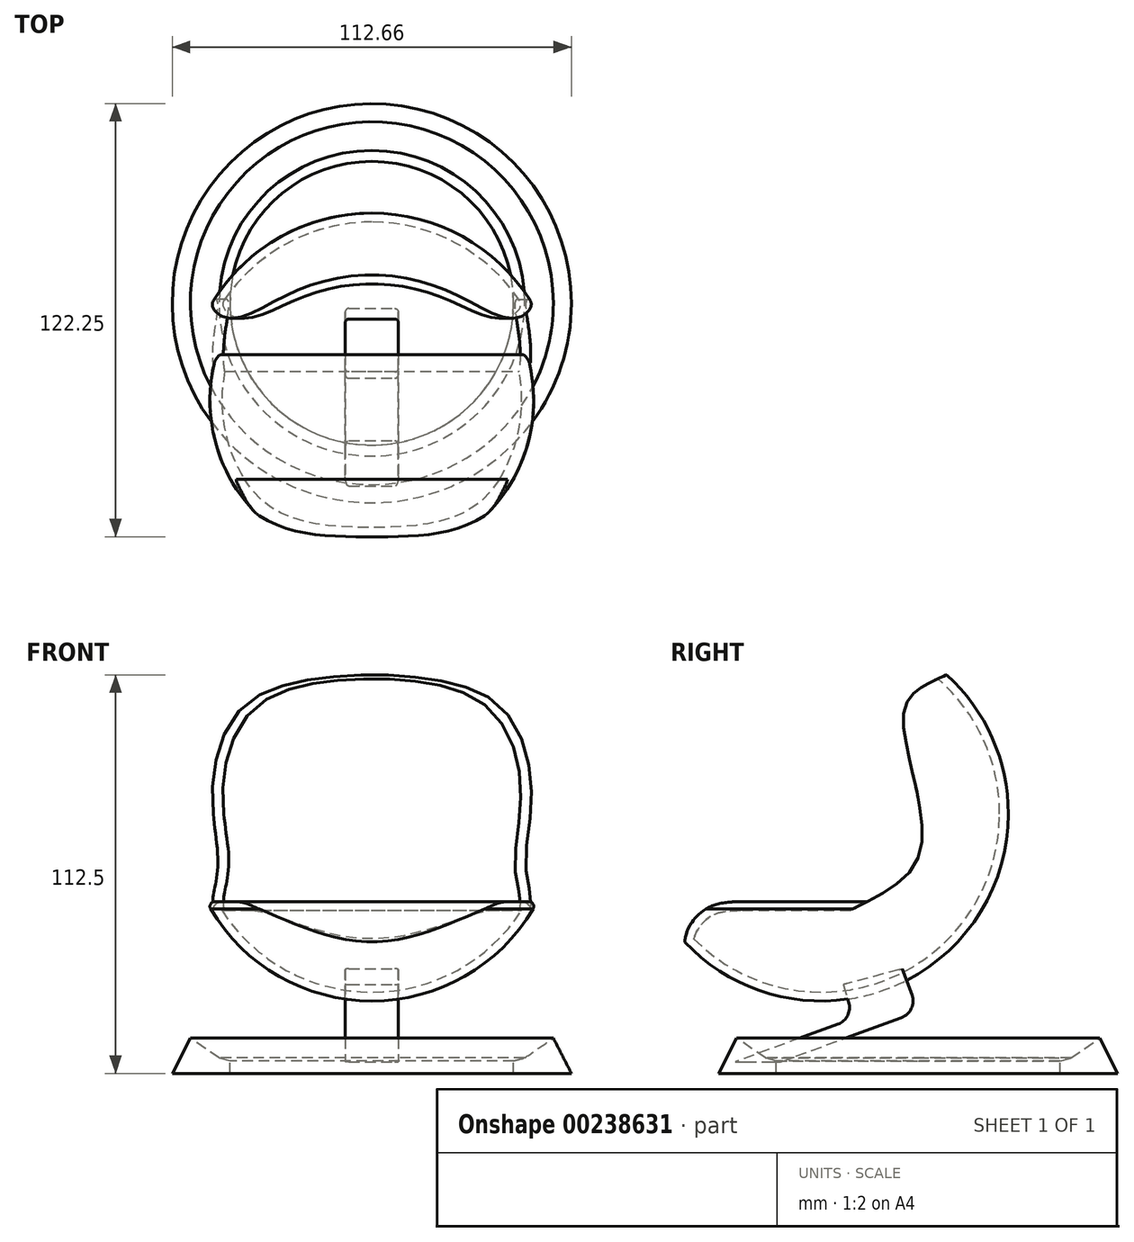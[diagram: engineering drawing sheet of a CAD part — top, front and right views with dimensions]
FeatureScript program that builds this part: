
annotation { "Feature Type Name" : "Feature", "Feature Type Description" : "" }
export const myFeature = defineFeature(function(context is Context, id is Id, definition is map)
    precondition{}
    {
        {
            var Q0;
            Q0=qCreatedBy(makeId("Top.planeOp"),FACE);
            var sketch = newSketch(context, id + "F0", { "sketchPlane" : qUnion([Q0])});
            skArc(sketch, "E0", {"start": v(0, 52.85) * mm, "mid": v(-52.85, 0) * mm, "end": v(0, -52.85) * mm});
            skLineSegment(sketch, "E1", {"start": v(0, -52.85) * mm, "end": v(0, 52.85) * mm});
            skSolve(sketch);
        }
        {
            var Q0;
            Q0=makeQuery(id+"F0.imprint","IMPRINT",FACE,{"disambiguationData":[TD([[makeQuery(id+"F0.imprint","IMPRINT",EDGE,{"derivedFrom":sQuery(id+"F0.wireOp",EDGE,"E0")}),1.0]])]});
            var Q1;
            Q1=sQuery(id+"F0.wireOp",EDGE,"E1");
            revolve(context, id + "F1", {"entities" : qUnion([Q0]), "axis" : qUnion([Q1]), "revolveType" : RevolveType.FULL});
        }
        {
            var Q0;
            Q0=qCreatedBy(makeId("Right.planeOp"),FACE);
            var sketch = newSketch(context, id + "F2", { "sketchPlane" : qUnion([Q0])});
            skFitSpline(sketch, "E2", {"points": [v(-34.6, -49.13) * mm, v(-38.42, -35.34) * mm, v(-31.97, -26.54) * mm, v(-22.3, -24.78) * mm], "startDerivative": vector(-18.06, 38.54) * mm, "endDerivative": vector(32.71, 0.77) * mm});
            skLineSegment(sketch, "E3", {"start": v(-22.3, -24.78) * mm, "end": v(12.9, -24.78) * mm});
            skFitSpline(sketch, "E4", {"points": [v(12.9, -24.78) * mm, v(28.16, -9.83) * mm, v(23.17, 26.54) * mm, v(28.74, 35.93) * mm, v(50.15, 44.43) * mm], "startDerivative": vector(83.43, 43.93) * mm, "endDerivative": vector(95.72, 31.54) * mm});
            skLineSegment(sketch, "E5", {"start": v(50.15, 44.43) * mm, "end": v(14.37, 64.97) * mm});
            skLineSegment(sketch, "E6", {"start": v(14.37, 64.97) * mm, "end": v(-80.66, 51.77) * mm});
            skLineSegment(sketch, "E7", {"start": v(-80.66, 51.77) * mm, "end": v(-54.55, -56.17) * mm});
            skLineSegment(sketch, "E8", {"start": v(-54.55, -56.17) * mm, "end": v(-34.6, -49.13) * mm});
            skSolve(sketch);
        }
        {
            var Q0;
            Q0=makeQuery(id+"F2.imprint","IMPRINT",FACE,{"disambiguationData":[TD([[makeQuery(id+"F2.imprint","IMPRINT",EDGE,{"derivedFrom":sQuery(id+"F2.wireOp",EDGE,"E2")}),1.0]])]});
            extrude(context, id + "F3", {"entities" : qUnion([Q0]), "operationType" : NewBodyOperationType.REMOVE, "oppositeDirection" : true, "depth" : 114 * mm, "symmetric" : true});
        }
        {
            var Q0;
            Q0=makeQuery(id+"F3.boolean.opBoolean","COPY",FACE,{"derivedFrom":makeQuery(id+"F3.opExtrude","SWEPT_FACE",FACE,{"disambiguationData":[OSD([sQuery(id+"F2.wireOp",EDGE,"E4")])]})});
            shell(context, id + "F4", {"entities" : qUnion([Q0]), "thickness" : 2.5 * mm});
        }
        {
            var Q0;
            Q0=qCreatedBy(makeId("Right.planeOp"),FACE);
            var sketch = newSketch(context, id + "F5", { "sketchPlane" : qUnion([Q0])});
            skLineSegment(sketch, "E9", {"start": v(6.26, -48.22) * mm, "end": v(9.16, -57.76) * mm});
            skLineSegment(sketch, "E10", {"start": v(9.16, -57.76) * mm, "end": v(-24.23, -70) * mm});
            skLineSegment(sketch, "E11", {"start": v(-24.23, -70) * mm, "end": v(-11.37, -70) * mm});
            skLineSegment(sketch, "E12", {"start": v(-11.37, -70) * mm, "end": v(27.35, -55.8) * mm});
            skLineSegment(sketch, "E13", {"start": v(27.35, -55.8) * mm, "end": v(22.92, -43.74) * mm});
            skLineSegment(sketch, "E14", {"start": v(22.92, -43.74) * mm, "end": v(6.26, -48.22) * mm});
            skSolve(sketch);
        }
        {
            var Q0;
            Q0=makeQuery(id+"F5.imprint","IMPRINT",FACE,{"disambiguationData":[TD([[makeQuery(id+"F5.imprint","IMPRINT",EDGE,{"derivedFrom":sQuery(id+"F5.wireOp",EDGE,"E9")}),1.0]])]});
            extrude(context, id + "F6", {"entities" : qUnion([Q0]), "oppositeDirection" : true, "depth" : 15 * mm, "offsetDistance" : 25 * mm, "symmetric" : true});
        }
        {
            var Q0;
            Q0=qCreatedBy(makeId("Right.planeOp"),FACE);
            var sketch = newSketch(context, id + "F7", { "sketchPlane" : qUnion([Q0])});
            skLineSegment(sketch, "E15", {"start": v(-15.73, -68.93) * mm, "end": v(-23.82, -63.33) * mm});
            skLineSegment(sketch, "E16", {"start": v(27.4, -61.47) * mm, "end": v(27.4, -83.03) * mm, "construction": true});
            skLineSegment(sketch, "E17", {"start": v(-12.64, -73.29) * mm, "end": v(-28.93, -73.29) * mm});
            skLineSegment(sketch, "E18", {"start": v(-28.93, -73.29) * mm, "end": v(-23.82, -63.33) * mm});
            skPoint(sketch, "E19.start.orphan", {"position": v(-23.82, -83.03) * mm});
            skLineSegment(sketch, "E20", {"start": v(-12.64, -73.29) * mm, "end": v(-12.64, -69.73) * mm});
            skLineSegment(sketch, "E21", {"start": v(-12.64, -69.73) * mm, "end": v(-15.73, -68.93) * mm});
            skSolve(sketch);
        }
        {
            var Q0;
            Q0=makeQuery(id+"F7.imprint","IMPRINT",FACE,{"disambiguationData":[TD([[makeQuery(id+"F7.imprint","IMPRINT",EDGE,{"derivedFrom":sQuery(id+"F7.wireOp",EDGE,"E15")}),1.0]])]});
            var Q1;
            Q1=sQuery(id+"F7.wireOp",EDGE,"E16");
            revolve(context, id + "F8", {"entities" : qUnion([Q0]), "axis" : qUnion([Q1]), "revolveType" : RevolveType.FULL});
        }
        {
            var Q0;
            Q0=makeQuery(id+"F6.opExtrude","SWEPT_EDGE",EDGE,{"disambiguationData":[OSD([sQuery(id+"F5.wireOp",EDGE,"E9"),sQuery(id+"F5.wireOp",EDGE,"E10")])]});
            var Q1;
            Q1=makeQuery(id+"F6.opExtrude","SWEPT_EDGE",EDGE,{"disambiguationData":[OSD([sQuery(id+"F5.wireOp",EDGE,"E12"),sQuery(id+"F5.wireOp",EDGE,"E13")])]});
            fillet(context, id + "F9", {"entities" : qUnion([Q0, Q1]), "radius" : 5 * mm, "tangentPropagation" : true, "allowEdgeOverflow" : false});
        }
        {
            var Q0;
            Q0=makeQuery(id+"F6.opExtrude","CAP_EDGE",EDGE,{"disambiguationData":[OSD([sQuery(id+"F5.wireOp",EDGE,"E13")])],"isStart":true});
            var Q1;
            {var subQ0=sQuery(id+"F5.wireOp",EDGE,"E10");var subQ1=sQuery(id+"F5.wireOp",EDGE,"E9");Q1=makeQuery(id+"F9.opFillet","BLEND_EDGE",EDGE,{"blendedFrom":[makeQuery(id+"F6.opExtrude","SWEPT_EDGE",EDGE,{"disambiguationData":[OSD([subQ1,subQ0])]}),makeQuery(id+"F6.opExtrude","CAP_FACE",FACE,{"disambiguationData":[OSD([subQ1,subQ0,sQuery(id+"F5.wireOp",EDGE,"E11"),sQuery(id+"F5.wireOp",EDGE,"E12"),sQuery(id+"F5.wireOp",EDGE,"E13"),sQuery(id+"F5.wireOp",EDGE,"E14")])],"isStart":true})],"blendedInto":[makeQuery(id+"F6.opExtrude","CAP_FACE",FACE,{"disambiguationData":[OSD([subQ1,subQ0,sQuery(id+"F5.wireOp",EDGE,"E11"),sQuery(id+"F5.wireOp",EDGE,"E12"),sQuery(id+"F5.wireOp",EDGE,"E13"),sQuery(id+"F5.wireOp",EDGE,"E14")])],"isStart":true})]});}
            var Q2;
            {var subQ0=sQuery(id+"F5.wireOp",EDGE,"E13");var subQ1=sQuery(id+"F5.wireOp",EDGE,"E12");Q2=makeQuery(id+"F9.opFillet","BLEND_EDGE",EDGE,{"blendedFrom":[makeQuery(id+"F6.opExtrude","SWEPT_EDGE",EDGE,{"disambiguationData":[OSD([subQ1,subQ0])]}),makeQuery(id+"F6.opExtrude","CAP_FACE",FACE,{"disambiguationData":[OSD([sQuery(id+"F5.wireOp",EDGE,"E9"),sQuery(id+"F5.wireOp",EDGE,"E10"),sQuery(id+"F5.wireOp",EDGE,"E11"),subQ1,subQ0,sQuery(id+"F5.wireOp",EDGE,"E14")])],"isStart":false})],"blendedInto":[makeQuery(id+"F6.opExtrude","CAP_FACE",FACE,{"disambiguationData":[OSD([sQuery(id+"F5.wireOp",EDGE,"E9"),sQuery(id+"F5.wireOp",EDGE,"E10"),sQuery(id+"F5.wireOp",EDGE,"E11"),subQ1,subQ0,sQuery(id+"F5.wireOp",EDGE,"E14")])],"isStart":false})]});}
            var Q3;
            {var subQ0=sQuery(id+"F5.wireOp",EDGE,"E10");var subQ1=sQuery(id+"F5.wireOp",EDGE,"E9");Q3=makeQuery(id+"F9.opFillet","BLEND_EDGE",EDGE,{"blendedFrom":[makeQuery(id+"F6.opExtrude","SWEPT_EDGE",EDGE,{"disambiguationData":[OSD([subQ1,subQ0])]}),makeQuery(id+"F6.opExtrude","CAP_FACE",FACE,{"disambiguationData":[OSD([subQ1,subQ0,sQuery(id+"F5.wireOp",EDGE,"E11"),sQuery(id+"F5.wireOp",EDGE,"E12"),sQuery(id+"F5.wireOp",EDGE,"E13"),sQuery(id+"F5.wireOp",EDGE,"E14")])],"isStart":false})],"blendedInto":[makeQuery(id+"F6.opExtrude","CAP_FACE",FACE,{"disambiguationData":[OSD([subQ1,subQ0,sQuery(id+"F5.wireOp",EDGE,"E11"),sQuery(id+"F5.wireOp",EDGE,"E12"),sQuery(id+"F5.wireOp",EDGE,"E13"),sQuery(id+"F5.wireOp",EDGE,"E14")])],"isStart":false})]});}
            fillet(context, id + "F10", {"entities" : qUnion([Q0, Q1, Q2, Q3]), "radius" : 1 * mm, "tangentPropagation" : true, "allowEdgeOverflow" : false});
        }
        {
            var Q0;
            Q0=makeQuery(id+"F3.boolean.opBoolean","INTERSECT",EDGE,{"disambiguationData":[OD(0.0)],"derivedFrom":[makeQuery(id+"F1.opRevolve","SWEPT_FACE",FACE,{"disambiguationData":[OSD([sQuery(id+"F0.wireOp",EDGE,"E0")])]}),makeQuery(id+"F3.opExtrude","SWEPT_FACE",FACE,{"disambiguationData":[OSD([sQuery(id+"F2.wireOp",EDGE,"E3")])]})]});
            var Q1;
            Q1=makeQuery(id+"F3.boolean.opBoolean","INTERSECT",EDGE,{"disambiguationData":[OD(1.0)],"derivedFrom":[makeQuery(id+"F1.opRevolve","SWEPT_FACE",FACE,{"disambiguationData":[OSD([sQuery(id+"F0.wireOp",EDGE,"E0")])]}),makeQuery(id+"F3.opExtrude","SWEPT_FACE",FACE,{"disambiguationData":[OSD([sQuery(id+"F2.wireOp",EDGE,"E3")])]})]});
            fillet(context, id + "F11", {"entities" : qUnion([Q0, Q1]), "radius" : 1.38 * mm, "tangentPropagation" : true, "allowEdgeOverflow" : false});
        }
    });
